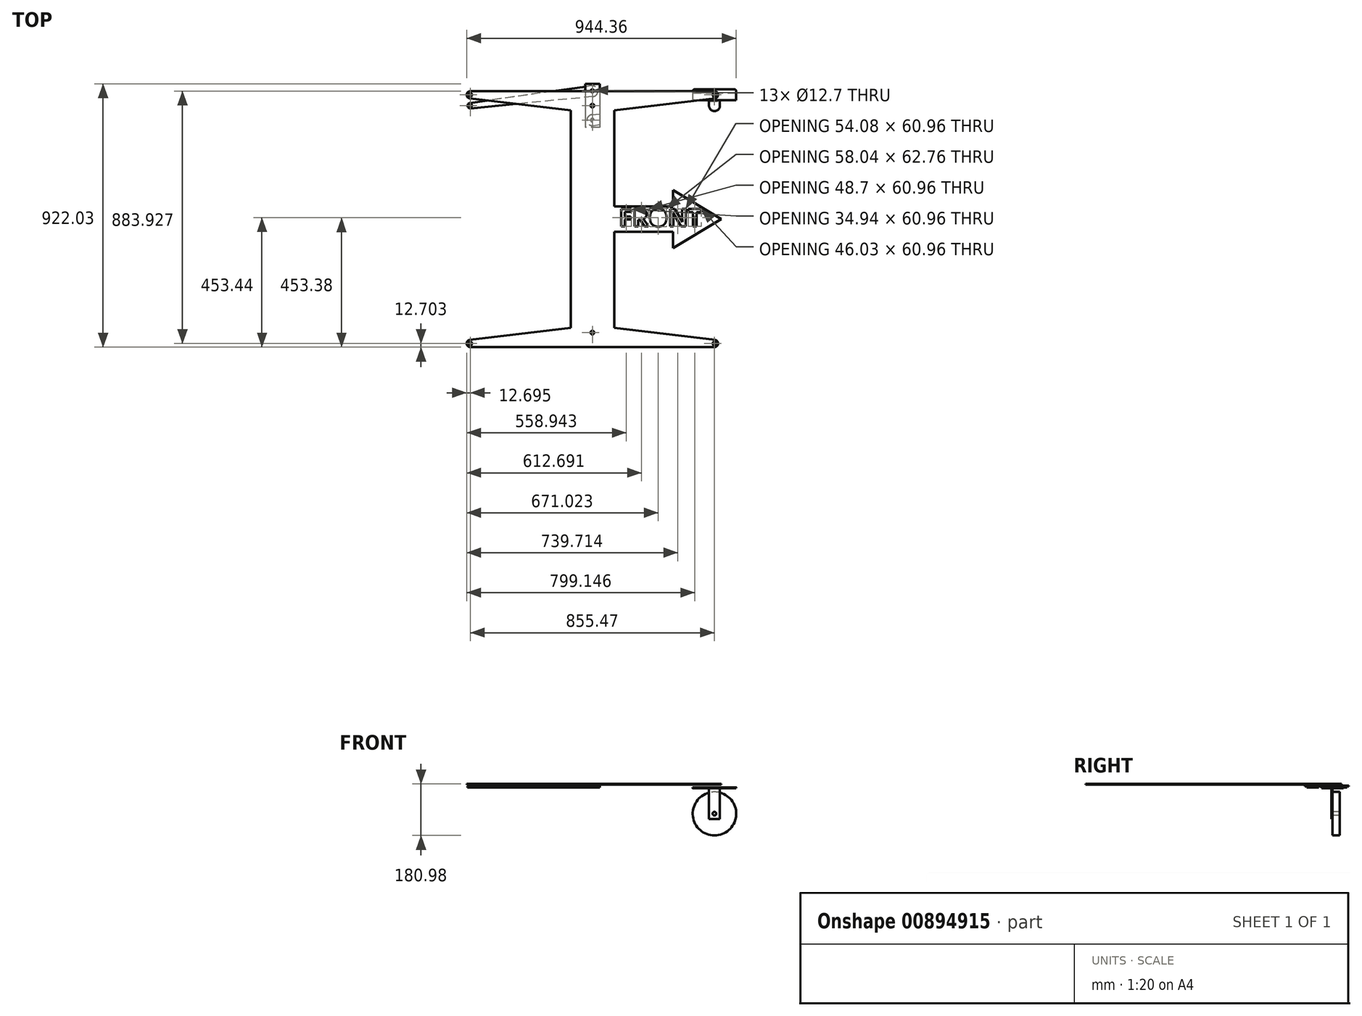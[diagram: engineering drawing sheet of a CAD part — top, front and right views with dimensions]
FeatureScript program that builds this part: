
annotation { "Feature Type Name" : "Feature", "Feature Type Description" : "" }
export const myFeature = defineFeature(function(context is Context, id is Id, definition is map)
    precondition{}
    {
        {
            var Q0;
            Q0=qCreatedBy(makeId("Top.planeOp"),FACE);
            var sketch = newSketch(context, id + "F0", { "sketchPlane" : qUnion([Q0])});
            skLineSegment(sketch, "E0.bottom", {"start": v(25.4, 76.2) * mm, "end": v(-25.4, 76.2) * mm});
            skLineSegment(sketch, "E0.top", {"start": v(25.4, -76.2) * mm, "end": v(-25.4, -76.2) * mm});
            skLineSegment(sketch, "E0.left", {"start": v(25.4, 76.2) * mm, "end": v(25.4, -76.2) * mm});
            skLineSegment(sketch, "E0.right", {"start": v(-25.4, 76.2) * mm, "end": v(-25.4, -76.2) * mm});
            skPoint(sketch, "E0.middle", {"position": v(0, 0) * mm});
            skCircle(sketch, "E1", {"center": v(0, -50.8) * mm, "radius": 6.35 * mm});
            skCircle(sketch, "E2", {"center": v(0, 50.8) * mm, "radius": 6.35 * mm});
            skPoint(sketch, "E2.centerSnap0", {"position": v(0, 76.2) * mm});
            skLineSegment(sketch, "E3", {"start": v(-2.66, 69.66) * mm, "end": v(-429.07, 9.43) * mm});
            skLineSegment(sketch, "E4", {"start": v(1.83, 31.84) * mm, "end": v(-426.82, -9.48) * mm});
            skArc(sketch, "E5", {"start": v(-2.66, 69.66) * mm, "mid": v(18.92, 53.05) * mm, "end": v(1.83, 31.84) * mm});
            skArc(sketch, "E6", {"start": v(-429.07, 9.43) * mm, "mid": v(-437.2, -1.12) * mm, "end": v(-426.82, -9.48) * mm});
            skLineSegment(sketch, "E7", {"start": v(-427.73, 0) * mm, "end": v(0, 50.8) * mm, "construction": true});
            skLineSegment(sketch, "E8", {"start": v(0, -50.8) * mm, "end": v(427.73, 0) * mm, "construction": true});
            skLineSegment(sketch, "E9", {"start": v(-1.83, -31.84) * mm, "end": v(426.82, 9.48) * mm});
            skLineSegment(sketch, "E10", {"start": v(2.66, -69.66) * mm, "end": v(429.07, -9.43) * mm});
            skArc(sketch, "E11", {"start": v(-1.83, -31.84) * mm, "mid": v(-18.92, -53.05) * mm, "end": v(2.66, -69.66) * mm});
            skArc(sketch, "E12", {"start": v(426.82, 9.48) * mm, "mid": v(437.2, 1.12) * mm, "end": v(429.07, -9.43) * mm});
            skCircle(sketch, "E13", {"center": v(427.73, 0) * mm, "radius": 6.35 * mm});
            skCircle(sketch, "E14", {"center": v(-427.73, 0) * mm, "radius": 6.35 * mm});
            skCircle(sketch, "E15", {"center": v(0, 0) * mm, "radius": 6.35 * mm});
            skSolve(sketch);
        }
        {
            var Q0;
            {var subQ11=sQuery(id+"F0.wireOp",EDGE,"E0.bottom");Q0=makeQuery(id+"F0.imprint","IMPRINT",FACE,{"disambiguationData":[TD([[makeQuery(id+"F0.imprint","IMPRINT",EDGE,{"derivedFrom":subQ11}),1.0]])]});}
            var Q1;
            Q1=makeQuery(id+"F0.imprint","IMPRINT",FACE,{"disambiguationData":[TD([[makeQuery(id+"F0.imprint","IMPRINT",EDGE,{"derivedFrom":sQuery(id+"F0.wireOp",EDGE,"E2")}),-1.0]])]});
            var Q2;
            Q2=makeQuery(id+"F0.imprint","IMPRINT",FACE,{"disambiguationData":[TD([[makeQuery(id+"F0.imprint","IMPRINT",EDGE,{"derivedFrom":sQuery(id+"F0.wireOp",EDGE,"E1")}),-1.0]])]});
            extrude(context, id + "F1", {"entities" : qUnion([Q0, Q1, Q2]), "depth" : 3.17 * mm, "offsetDistance" : 25.4 * mm});
        }
        {
            var Q0;
            {var subQ0=sQuery(id+"F0.wireOp",EDGE,"E12");Q0=makeQuery(id+"F0.imprint","IMPRINT",FACE,{"disambiguationData":[TD([[makeQuery(id+"F0.imprint","IMPRINT",EDGE,{"derivedFrom":subQ0}),-1.0]])]});}
            var Q1;
            {var subQ0=sQuery(id+"F0.wireOp",EDGE,"E6");Q1=makeQuery(id+"F0.imprint","IMPRINT",FACE,{"disambiguationData":[TD([[makeQuery(id+"F0.imprint","IMPRINT",EDGE,{"derivedFrom":subQ0}),1.0]])]});}
            var Q2;
            Q2=makeQuery(id+"F0.imprint","IMPRINT",FACE,{"disambiguationData":[TD([[makeQuery(id+"F0.imprint","IMPRINT",EDGE,{"derivedFrom":sQuery(id+"F0.wireOp",EDGE,"E2")}),-1.0]])]});
            var Q3;
            Q3=makeQuery(id+"F0.imprint","IMPRINT",FACE,{"disambiguationData":[TD([[makeQuery(id+"F0.imprint","IMPRINT",EDGE,{"derivedFrom":sQuery(id+"F0.wireOp",EDGE,"E1")}),-1.0]])]});
            extrude(context, id + "F2", {"entities" : qUnion([Q0, Q1, Q2, Q3]), "oppositeDirection" : true, "depth" : 3.17 * mm, "offsetDistance" : 25.4 * mm});
        }
        {
            var Q0;
            Q0=makeQuery(id+"F2.opExtrude","CAP_FACE",FACE,{"disambiguationData":[OSD([sQuery(id+"F0.wireOp",EDGE,"E1"),sQuery(id+"F0.wireOp",EDGE,"E9"),sQuery(id+"F0.wireOp",EDGE,"E10"),sQuery(id+"F0.wireOp",EDGE,"E11"),sQuery(id+"F0.wireOp",EDGE,"E12"),sQuery(id+"F0.wireOp",EDGE,"E13")])],"isStart":false});
            var sketch = newSketch(context, id + "F3", { "sketchPlane" : qUnion([Q0])});
            skCircle(sketch, "E16.0", {"center": v(427.73, 0) * mm, "radius": 6.35 * mm});
            skCircle(sketch, "E17.0", {"center": v(0, 0) * mm, "radius": 6.35 * mm});
            skLineSegment(sketch, "E18", {"start": v(427.73, 0) * mm, "end": v(427.73, -38.1) * mm, "construction": true});
            skCircle(sketch, "E19", {"center": v(427.73, -38.1) * mm, "radius": 6.35 * mm});
            skLineSegment(sketch, "E20", {"start": v(446.78, 0) * mm, "end": v(446.78, -38.1) * mm});
            skLineSegment(sketch, "E21", {"start": v(408.68, 0) * mm, "end": v(408.68, -38.1) * mm});
            skArc(sketch, "E22", {"start": v(446.78, -38.1) * mm, "mid": v(427.73, -57.15) * mm, "end": v(408.68, -38.1) * mm});
            skArc(sketch, "E23", {"start": v(446.78, 0) * mm, "mid": v(427.73, 19.05) * mm, "end": v(408.68, 0) * mm});
            skLineSegment(sketch, "E24", {"start": v(427.73, 0) * mm, "end": v(0, 0) * mm, "construction": true});
            skLineSegment(sketch, "E25.bottom", {"start": v(357.88, -57.15) * mm, "end": v(497.58, -57.15) * mm});
            skLineSegment(sketch, "E25.top", {"start": v(357.88, -19.05) * mm, "end": v(497.58, -19.05) * mm});
            skLineSegment(sketch, "E25.left", {"start": v(351.53, -50.8) * mm, "end": v(351.53, -25.4) * mm});
            skLineSegment(sketch, "E25.right", {"start": v(503.93, -50.8) * mm, "end": v(503.93, -25.4) * mm});
            skPoint(sketch, "E26.visualSharp", {"position": v(351.53, -57.15) * mm});
            skArc(sketch, "E26.filletArc", {"start": v(351.53, -50.8) * mm, "mid": v(353.4, -55.3) * mm, "end": v(357.88, -57.15) * mm});
            skPoint(sketch, "E27.visualSharp", {"position": v(351.53, -19.05) * mm});
            skArc(sketch, "E27.filletArc", {"start": v(357.88, -19.05) * mm, "mid": v(353.4, -20.9) * mm, "end": v(351.53, -25.4) * mm});
            skPoint(sketch, "E28.visualSharp", {"position": v(503.93, -57.15) * mm});
            skArc(sketch, "E28.filletArc", {"start": v(497.58, -57.15) * mm, "mid": v(502.08, -55.3) * mm, "end": v(503.93, -50.8) * mm});
            skPoint(sketch, "E29.visualSharp", {"position": v(503.93, -19.05) * mm});
            skArc(sketch, "E29.filletArc", {"start": v(503.93, -25.4) * mm, "mid": v(502.08, -20.9) * mm, "end": v(497.58, -19.05) * mm});
            skSolve(sketch);
        }
        {
            var Q0;
            Q0=makeQuery(id+"F3.imprint","IMPRINT",FACE,{"disambiguationData":[TD([[makeQuery(id+"F3.imprint","IMPRINT",EDGE,{"derivedFrom":sQuery(id+"F3.wireOp",EDGE,"E16.0")}),1.0]])]});
            var Q1;
            {var subQ3=sQuery(id+"F3.wireOp",EDGE,"E21");var subQ5=sQuery(id+"F3.wireOp",EDGE,"E22");var subQ6=makeQuery(id+"F3.imprint","INTERSECT",VERTEX,{"derivedFrom":[subQ3,subQ5]});Q1=makeQuery(id+"F3.imprint","IMPRINT",FACE,{"disambiguationData":[TD([[makeQuery(id+"F3.imprint","IMPRINT",EDGE,{"disambiguationData":[TD([[subQ6,1.0]])],"derivedFrom":subQ3}),1.0]])]});}
            var Q2;
            Q2=makeQuery(id+"F3.imprint","IMPRINT",FACE,{"disambiguationData":[TD([[makeQuery(id+"F3.imprint","IMPRINT",EDGE,{"derivedFrom":sQuery(id+"F3.wireOp",EDGE,"E25.left")}),-1.0]])]});
            var Q3;
            Q3=makeQuery(id+"F3.imprint","IMPRINT",FACE,{"disambiguationData":[TD([[makeQuery(id+"F3.imprint","IMPRINT",EDGE,{"derivedFrom":sQuery(id+"F3.wireOp",EDGE,"E19")}),-1.0]])]});
            var Q4;
            {var subQ0=sQuery(id+"F3.wireOp",EDGE,"E22");var subQ1=sQuery(id+"F3.wireOp",EDGE,"E21");var subQ2=makeQuery(id+"F3.imprint","INTERSECT",VERTEX,{"derivedFrom":[subQ1,subQ0]});Q4=makeQuery(id+"F3.imprint","IMPRINT",FACE,{"disambiguationData":[TD([[makeQuery(id+"F3.imprint","IMPRINT",EDGE,{"disambiguationData":[TD([[subQ2,1.0]])],"derivedFrom":subQ1}),-1.0]])]});}
            var Q5;
            {var subQ1=sQuery(id+"F3.wireOp",EDGE,"E20");Q5=makeQuery(id+"F3.imprint","IMPRINT",FACE,{"disambiguationData":[TD([[makeQuery(id+"F3.imprint","IMPRINT",EDGE,{"derivedFrom":subQ1}),1.0]])]});}
            var Q6;
            {var subQ1=sQuery(id+"F3.wireOp",EDGE,"E23");var subQ7=sQuery(id+"F3.wireOp",EDGE,"E21");var subQ9=makeQuery(id+"F3.imprint","INTERSECT",VERTEX,{"derivedFrom":[subQ7,subQ1]});Q6=makeQuery(id+"F3.imprint","IMPRINT",FACE,{"disambiguationData":[TD([[makeQuery(id+"F3.imprint","IMPRINT",EDGE,{"disambiguationData":[TD([[subQ9,-1.0]])],"derivedFrom":subQ7}),1.0]])]});}
            var Q7;
            {var subQ0=sQuery(id+"F3.wireOp",EDGE,"E25.top");var subQ1=sQuery(id+"F3.wireOp",EDGE,"E21");var subQ2=makeQuery(id+"F3.imprint","INTERSECT",VERTEX,{"derivedFrom":[subQ1,subQ0]});Q7=makeQuery(id+"F3.imprint","IMPRINT",FACE,{"disambiguationData":[TD([[makeQuery(id+"F3.imprint","IMPRINT",EDGE,{"disambiguationData":[TD([[subQ2,1.0]])],"derivedFrom":subQ1}),1.0]])]});}
            var Q8;
            {var subQ0=sQuery(id+"F3.wireOp",EDGE,"E25.top");var subQ1=makeQuery(id+"F2.opExtrude","CAP_EDGE",EDGE,{"disambiguationData":[OSD([sQuery(id+"F0.wireOp",EDGE,"E9")])],"isStart":false});var subQ2=makeQuery(id+"F3.imprint","INTERSECT",VERTEX,{"derivedFrom":[subQ1,subQ0]});Q8=makeQuery(id+"F3.imprint","IMPRINT",FACE,{"disambiguationData":[TD([[makeQuery(id+"F3.imprint","IMPRINT",EDGE,{"disambiguationData":[TD([[subQ2,-1.0]])],"derivedFrom":subQ0}),-1.0]])]});}
            extrude(context, id + "F4", {"entities" : qUnion([Q0, Q1, Q2, Q3, Q4, Q5, Q6, Q7, Q8]), "depth" : 3.17 * mm, "offsetDistance" : 25.4 * mm});
        }
        {
            var Q0;
            Q0=makeQuery(id+"F1.opExtrude","CAP_FACE",FACE,{"disambiguationData":[OSD([sQuery(id+"F0.wireOp",EDGE,"E0.bottom"),sQuery(id+"F0.wireOp",EDGE,"E0.top"),sQuery(id+"F0.wireOp",EDGE,"E0.left"),sQuery(id+"F0.wireOp",EDGE,"E0.right"),sQuery(id+"F0.wireOp",EDGE,"E1"),sQuery(id+"F0.wireOp",EDGE,"E2"),sQuery(id+"F0.wireOp",EDGE,"E15")])],"isStart":false});
            cPlane(context, id + "F5", {"entities" : qUnion([Q0]), "cplaneType" : CPlaneType.OFFSET, "offset" : 3.17 * mm, "width" : 152.4 * mm, "height" : 152.4 * mm});
        }
        {
            var Q0;
            Q0=qCreatedBy(id+"F5.planeOp",FACE);
            var sketch = newSketch(context, id + "F6", { "sketchPlane" : qUnion([Q0])});
            skCircle(sketch, "E30.0", {"center": v(0, 0) * mm, "radius": 6.35 * mm});
            skCircle(sketch, "E31.0", {"center": v(427.73, 38.1) * mm, "radius": 6.35 * mm});
            skCircle(sketch, "E32.0", {"center": v(-427.73, 0) * mm, "radius": 6.35 * mm});
            skLineSegment(sketch, "E33", {"start": v(3, -25.22) * mm, "end": v(429.24, 25.49) * mm});
            skLineSegment(sketch, "E34", {"start": v(427.73, 50.8) * mm, "end": v(-427.73, 50.8) * mm});
            skLineSegment(sketch, "E35", {"start": v(-3, -25.22) * mm, "end": v(-429.24, 25.49) * mm});
            skLineSegment(sketch, "E36", {"start": v(0, 6.35) * mm, "end": v(0, 242.01) * mm, "construction": true});
            skCircle(sketch, "E37.MirrorC", {"center": v(-427.73, 38.1) * mm, "radius": 6.35 * mm});
            skArc(sketch, "E38", {"start": v(427.73, 50.8) * mm, "mid": v(440.41, 38.85) * mm, "end": v(429.24, 25.49) * mm});
            skArc(sketch, "E39", {"start": v(-429.24, 25.49) * mm, "mid": v(-440.41, 38.85) * mm, "end": v(-427.73, 50.8) * mm});
            skPoint(sketch, "E40.visualSharp", {"position": v(0, -25.58) * mm});
            skArc(sketch, "E40.filletArc", {"start": v(-3, -25.22) * mm, "mid": v(0, -25.4) * mm, "end": v(3, -25.22) * mm});
            skLineSegment(sketch, "E41.bottom", {"start": v(76.2, -16.51) * mm, "end": v(-76.2, -16.51) * mm});
            skLineSegment(sketch, "E41.top", {"start": v(76.2, -778.51) * mm, "end": v(-76.2, -778.51) * mm});
            skLineSegment(sketch, "E41.left", {"start": v(76.2, -16.51) * mm, "end": v(76.2, -778.51) * mm});
            skLineSegment(sketch, "E41.right", {"start": v(-76.2, -16.51) * mm, "end": v(-76.2, -778.51) * mm});
            skPoint(sketch, "E42", {"position": v(0, -16.51) * mm});
            skLineSegment(sketch, "E43", {"start": v(-76.2, -397.51) * mm, "end": v(76.2, -397.51) * mm, "construction": true});
            skLineSegment(sketch, "E44.MirrorCS", {"start": v(3, -769.8) * mm, "end": v(429.24, -820.52) * mm});
            skArc(sketch, "E45.MirrorCS", {"start": v(427.73, -845.83) * mm, "mid": v(440.41, -833.88) * mm, "end": v(429.24, -820.52) * mm});
            skCircle(sketch, "E46.MirrorC", {"center": v(427.73, -833.13) * mm, "radius": 6.35 * mm});
            skLineSegment(sketch, "E47.MirrorCS", {"start": v(427.73, -845.83) * mm, "end": v(-427.73, -845.83) * mm});
            skArc(sketch, "E48.MirrorCS", {"start": v(-3, -769.8) * mm, "mid": v(0, -769.63) * mm, "end": v(3, -769.8) * mm});
            skLineSegment(sketch, "E49.MirrorCS", {"start": v(-3, -769.8) * mm, "end": v(-429.24, -820.52) * mm});
            skArc(sketch, "E50.MirrorCS", {"start": v(-429.24, -820.52) * mm, "mid": v(-440.41, -833.88) * mm, "end": v(-427.73, -845.83) * mm});
            skCircle(sketch, "E51.MirrorC", {"center": v(-427.73, -833.13) * mm, "radius": 6.35 * mm});
            skCircle(sketch, "E52.MirrorC", {"center": v(0, -795.03) * mm, "radius": 6.35 * mm});
            skLineSegment(sketch, "E53.bottom", {"start": v(76.2, -441.98) * mm, "end": v(283, -441.98) * mm});
            skLineSegment(sketch, "E53.top", {"start": v(76.2, -353.04) * mm, "end": v(283, -353.04) * mm});
            skLineSegment(sketch, "E53.left", {"start": v(76.2, -441.98) * mm, "end": v(76.2, -353.04) * mm});
            skLineSegment(sketch, "E53.right", {"start": v(283, -441.98) * mm, "end": v(283, -353.04) * mm});
            skLineSegment(sketch, "E54", {"start": v(283, -441.98) * mm, "end": v(283, -499.22) * mm});
            skLineSegment(sketch, "E55", {"start": v(283, -499.22) * mm, "end": v(451.84, -397.51) * mm});
            skLineSegment(sketch, "E56", {"start": v(451.84, -397.51) * mm, "end": v(283, -295.8) * mm});
            skLineSegment(sketch, "E57", {"start": v(283, -295.8) * mm, "end": v(283, -353.04) * mm});
            skText(sketch, "E58", { "text": "FRONT", "fontName": "OpenSans-Bold.ttf"});
            const initialGuessF6  = {"E58": [0.09337, -0.42293, 1, 0, 0.06148]};
            skSetInitialGuess(sketch, initialGuessF6);
            skSolve(sketch);
        }
        {
            var Q0;
            Q0=makeQuery(id+"F6.imprint","IMPRINT",FACE,{"disambiguationData":[TD([[makeQuery(id+"F6.imprint","IMPRINT",EDGE,{"derivedFrom":sQuery(id+"F6.wireOp",EDGE,"E30.0")}),-1.0]])]});
            var Q1;
            {var subQ0=sQuery(id+"F6.wireOp",EDGE,"E40.filletArc");Q1=makeQuery(id+"F6.imprint","IMPRINT",FACE,{"disambiguationData":[TD([[makeQuery(id+"F6.imprint","IMPRINT",EDGE,{"derivedFrom":subQ0}),-1.0]])]});}
            var Q2;
            {var subQ2=sQuery(id+"F6.wireOp",EDGE,"E40.filletArc");Q2=makeQuery(id+"F6.imprint","IMPRINT",FACE,{"disambiguationData":[TD([[makeQuery(id+"F6.imprint","IMPRINT",EDGE,{"derivedFrom":subQ2}),1.0]])]});}
            var Q3;
            {var subQ2=sQuery(id+"F6.wireOp",EDGE,"E41.top");Q3=makeQuery(id+"F6.imprint","IMPRINT",FACE,{"disambiguationData":[TD([[makeQuery(id+"F6.imprint","IMPRINT",EDGE,{"derivedFrom":subQ2}),1.0]])]});}
            var Q4;
            {var subQ0=sQuery(id+"F6.wireOp",EDGE,"E41.top");Q4=makeQuery(id+"F6.imprint","IMPRINT",FACE,{"disambiguationData":[TD([[makeQuery(id+"F6.imprint","IMPRINT",EDGE,{"derivedFrom":subQ0}),-1.0]])]});}
            var Q5;
            {var subQ4=sQuery(id+"F6.wireOp",EDGE,"E53.bottom");Q5=makeQuery(id+"F6.imprint","IMPRINT",FACE,{"disambiguationData":[TD([[makeQuery(id+"F6.imprint","IMPRINT",EDGE,{"derivedFrom":subQ4}),1.0]])]});}
            var Q6;
            {var subQ9=sQuery(id+"F6.wireOp",EDGE,"E54");Q6=makeQuery(id+"F6.imprint","IMPRINT",FACE,{"disambiguationData":[TD([[makeQuery(id+"F6.imprint","IMPRINT",EDGE,{"derivedFrom":subQ9}),1.0]])]});}
            extrude(context, id + "F7", {"entities" : qUnion([Q0, Q1, Q2, Q3, Q4, Q5, Q6]), "depth" : 3.17 * mm, "offsetDistance" : 25.4 * mm});
        }
        {
            var Q0;
            {var subQ0=sQuery(id+"F3.wireOp",EDGE,"E25.top");Q0=makeQuery(id+"F4.opExtrude","SWEPT_FACE",FACE,{"disambiguationData":[OSD([subQ0]),TDD([makeQuery(id+"F3.imprint","IMPRINT",EDGE,{"disambiguationData":[TD([[makeQuery(id+"F3.imprint","INTERSECT",VERTEX,{"derivedFrom":[subQ0,sQuery(id+"F3.wireOp",EDGE,"E29.filletArc")]}),1.0]])],"derivedFrom":subQ0})])]});}
            var sketch = newSketch(context, id + "F8", { "sketchPlane" : qUnion([Q0])});
            skLineSegment(sketch, "E59.0.0", {"start": v(497.58, -3.18) * mm, "end": v(446.78, -3.18) * mm, "construction": true});
            skLineSegment(sketch, "E59.0.1", {"start": v(446.78, -3.18) * mm, "end": v(446.78, -6.35) * mm, "construction": true});
            skLineSegment(sketch, "E59.0.2", {"start": v(446.78, -6.35) * mm, "end": v(497.58, -6.35) * mm, "construction": true});
            skLineSegment(sketch, "E59.0.3", {"start": v(497.58, -6.35) * mm, "end": v(497.58, -3.18) * mm, "construction": true});
            skLineSegment(sketch, "E60.0.0", {"start": v(408.68, -3.18) * mm, "end": v(357.88, -3.18) * mm, "construction": true});
            skLineSegment(sketch, "E60.0.1", {"start": v(357.88, -3.18) * mm, "end": v(357.88, -6.35) * mm, "construction": true});
            skLineSegment(sketch, "E60.0.2", {"start": v(357.88, -6.35) * mm, "end": v(408.68, -6.35) * mm, "construction": true});
            skLineSegment(sketch, "E60.0.3", {"start": v(408.68, -6.35) * mm, "end": v(408.68, -3.18) * mm, "construction": true});
            skLineSegment(sketch, "E61.bottom", {"start": v(408.68, -6.35) * mm, "end": v(446.78, -6.35) * mm});
            skLineSegment(sketch, "E61.top", {"start": v(408.68, -114.3) * mm, "end": v(446.78, -114.3) * mm});
            skLineSegment(sketch, "E61.left", {"start": v(408.68, -6.35) * mm, "end": v(408.68, -114.3) * mm});
            skLineSegment(sketch, "E61.right", {"start": v(446.78, -6.35) * mm, "end": v(446.78, -114.3) * mm});
            skCircle(sketch, "E62", {"center": v(427.73, -95.25) * mm, "radius": 6.35 * mm});
            skPoint(sketch, "E62.centerSnap0", {"position": v(427.73, -114.3) * mm});
            skCircle(sketch, "E63", {"center": v(427.73, -95.25) * mm, "radius": 76.2 * mm});
            skSolve(sketch);
        }
        {
            var Q0;
            {var subQ1=sQuery(id+"F8.wireOp",EDGE,"E61.top");Q0=makeQuery(id+"F8.imprint","IMPRINT",FACE,{"disambiguationData":[TD([[makeQuery(id+"F8.imprint","IMPRINT",EDGE,{"derivedFrom":subQ1}),1.0]])]});}
            var Q1;
            {var subQ0=sQuery(id+"F8.wireOp",EDGE,"E61.bottom");Q1=makeQuery(id+"F8.imprint","IMPRINT",FACE,{"disambiguationData":[TD([[makeQuery(id+"F8.imprint","IMPRINT",EDGE,{"derivedFrom":subQ0}),-1.0]])]});}
            extrude(context, id + "F9", {"entities" : qUnion([Q0, Q1]), "operationType" : NewBodyOperationType.ADD, "depth" : 3.17 * mm, "offsetDistance" : 25.4 * mm});
        }
        {
            var Q0;
            {var subQ0=sQuery(id+"F8.wireOp",EDGE,"E61.top");Q0=makeQuery(id+"F8.imprint","IMPRINT",FACE,{"disambiguationData":[TD([[makeQuery(id+"F8.imprint","IMPRINT",EDGE,{"derivedFrom":subQ0}),-1.0]])]});}
            var Q1;
            {var subQ1=sQuery(id+"F8.wireOp",EDGE,"E61.top");Q1=makeQuery(id+"F8.imprint","IMPRINT",FACE,{"disambiguationData":[TD([[makeQuery(id+"F8.imprint","IMPRINT",EDGE,{"derivedFrom":subQ1}),1.0]])]});}
            extrude(context, id + "F10", {"entities" : qUnion([Q0, Q1]), "oppositeDirection" : true, "depth" : 25.4 * mm, "offsetDistance" : 25.4 * mm});
        }
    });
